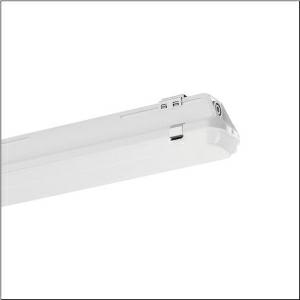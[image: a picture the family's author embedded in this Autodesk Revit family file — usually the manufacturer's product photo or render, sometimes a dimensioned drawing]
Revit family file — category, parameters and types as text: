
# Revit family: monsun_11_emergency_51fp207p467l3g
name_source: partatom
category: Lighting Fixtures
units: mm (PartAtom-declared; Revit-internal decimal feet)

## family parameters
Cut with Voids When Loaded = No
Host = Face
Light Source = No
Part Type = Normal
Room Calculation Point = No
Round Connector Dimension = Use Diameter
Shared = No

## types (1)
- --- (1 x LED, 890 lm, 6.5 W, 4000K)
    Apparent Load = 7 VA
    CIE Flux Codes = 45 75 93 94 100
    Color Rendering = 80
    Color Temperature = 4000K
    Default Elevation = 1800 mm
    Description = Monsun 11 emergency, damp-proof luminaire, chain hanger, primary optical cover: enclosure, of PC, light emission: direct distribution, primary light characteristic: symmetric, installation type: suspended mounting, surface-mounted, horizontal mounting, vertical mounting, LED, rated luminous flux: 5.450lm, luminous efficacy: 161lm/W, light colour: 840, colour temperature: 4000K, control gear: ON/OFF, with terminal, 4-pole, max. 2.5mm², mains connection: 220..240V, AC, 50/60Hz, rated input power: 37W, control gear: single battery element, battery: LiFePO4, 9Ah, luminaire housing, of glass-fibre reinforced polyester, uncoated, bright grey, incl. chain hanger, length: 1.590mm, width: 90mm, height: 88mm, clip for enclosure, of stainless steel (V2A), ceiling mounting element, of stainless steel (V2A), chain hanger, of stainless steel (V2A), protection rating (complete): IP66, insulation class (complete): insulation class I (protective earthing), certification: CE, UKCA, protection symbol: D, impact resistance: IK08, permissible operating ambient temperature: +5..+35°C, standard: EN 50419, EN 60598-2-1, EN 60598-2-22, contact your sales advisor before using the luminaires in applications with unclear chemical exposure, large temperature fluctuations or condensation-forming humidity, LABS conformity tested according to VDMA 24364:2018-05, no direct snow, no direct sun, no direct rain, for indoor or canopied outdoor use, corresponds to IFS (International Featured Standards) requirements for safety and quality in the food industry, packaging unit: 1 piece
    Height = 89 mm
    Lamp = 1 x LED
    Lamp Light Flux = 890 lm
    Lamp Power = 6.5 W
    Lamp count = 1
    Length = 1590 mm
    Luminous efficacy = 137 lm/W
    Manufacturer = Siteco
    ModVariant = No
    Model = 51FP207P467L3G
    Mounting Place = Ceiling
    Mounting Type = Surface mounted
    Number of Poles = 1
    OnlyDefault = Yes
    Power Factor = 1
    Product Name = Monsun 11 emergency
    Product group = damp-proof luminaire
    ProductGroupID = 300
    Protection Class = Protection class I
    Protection Degree = IP 66
    RLX_Detail_Level = 1
    RLX_Emergency_Light_Flux = 0 lm
    RLX_Emergency_Type = 0
    RLX_Emergency_Type_DB = No
    RlxData = <blob elided: 88621 chars, md5=21755d4e>
    Socket = socket
    Standby Power = 0 W
    System Light Flux = 890 lm
    System Power = 7 W
    Type Comments = : emergency light operation: 3 h
    Type Image = l_1349237.jpg
    URL = http://relux.com
    VarID = @adj_034289
    Voltage = 0 V
    Weight = 0.00 kg
    Width = 90 mm

## geometry (parser evidence)
native form markers: Blend x4, Sweep x14
no freeform markers — native parametric forms only
